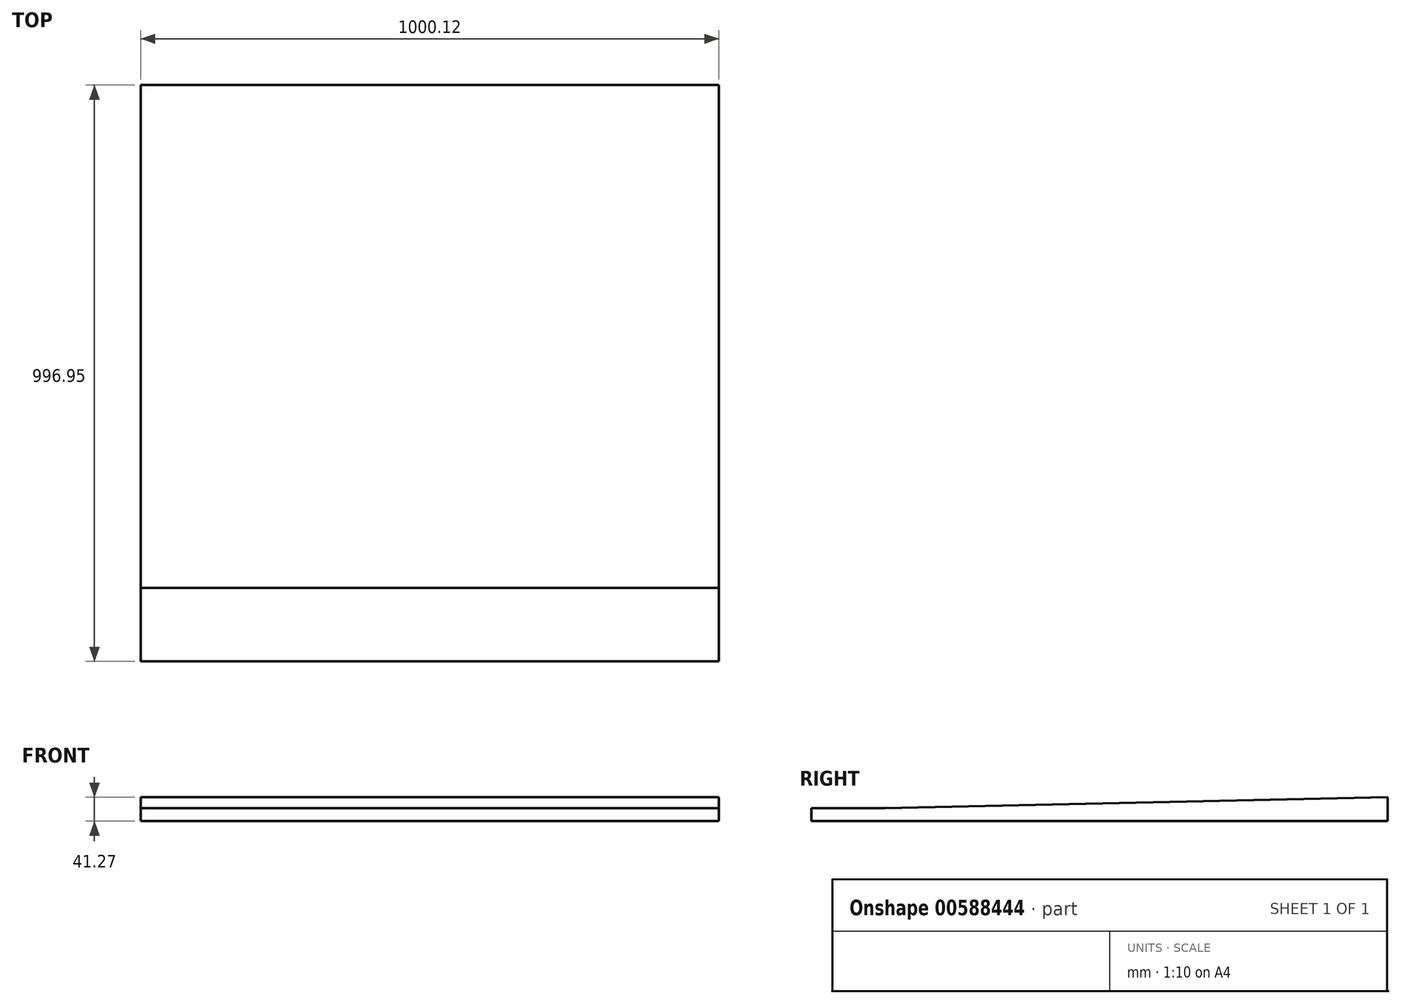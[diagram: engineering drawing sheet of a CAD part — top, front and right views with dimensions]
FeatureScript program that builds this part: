
annotation { "Feature Type Name" : "Feature", "Feature Type Description" : "" }
export const myFeature = defineFeature(function(context is Context, id is Id, definition is map)
    precondition{}
    {
        {
            var Q0;
            Q0=qCreatedBy(makeId("Right.planeOp"),FACE);
            var sketch = newSketch(context, id + "F0", { "sketchPlane" : qUnion([Q0])});
            skLineSegment(sketch, "E0", {"start": v(0, 0) * mm, "end": v(996.95, 0) * mm});
            skLineSegment(sketch, "E1", {"start": v(996.95, 0) * mm, "end": v(996.95, 41.28) * mm});
            skLineSegment(sketch, "E2", {"start": v(996.95, 41.28) * mm, "end": v(127, 22.22) * mm});
            skLineSegment(sketch, "E3", {"start": v(127, 22.23) * mm, "end": v(0, 22.23) * mm});
            skLineSegment(sketch, "E4", {"start": v(0, 22.23) * mm, "end": v(0, 0) * mm});
            skSolve(sketch);
        }
        {
            var Q0;
            Q0=makeQuery(id+"F0.imprint","IMPRINT",FACE,{"disambiguationData":[TD([[makeQuery(id+"F0.imprint","IMPRINT",EDGE,{"derivedFrom":sQuery(id+"F0.wireOp",EDGE,"E0")}),1.0]])]});
            extrude(context, id + "F1", {"entities" : qUnion([Q0]), "depth" : 1000.12 * mm, "offsetDistance" : 25.4 * mm});
        }
    });
